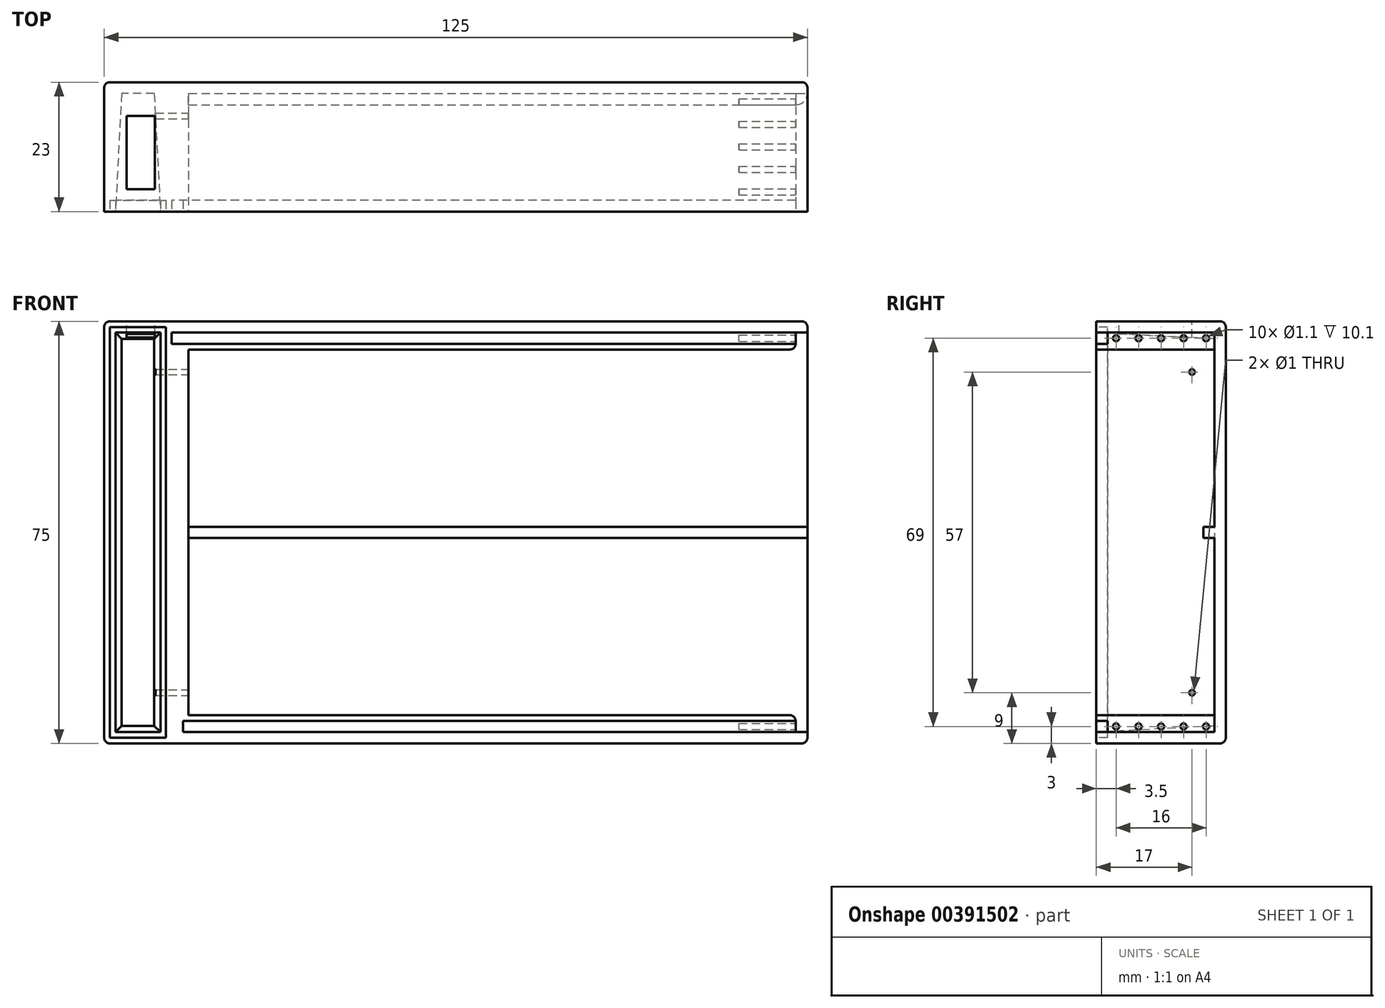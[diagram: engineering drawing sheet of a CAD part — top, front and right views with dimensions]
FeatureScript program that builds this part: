
annotation { "Feature Type Name" : "Feature", "Feature Type Description" : "" }
export const myFeature = defineFeature(function(context is Context, id is Id, definition is map)
    precondition{}
    {
        {
            var Q0;
            Q0=qCreatedBy(makeId("Front.planeOp"),FACE);
            var sketch = newSketch(context, id + "F0", { "sketchPlane" : qUnion([Q0])});
            skLineSegment(sketch, "E0.bottom", {"start": v(-62.5, 37.5) * mm, "end": v(62.5, 37.5) * mm});
            skLineSegment(sketch, "E0.top", {"start": v(-62.5, -37.5) * mm, "end": v(62.5, -37.5) * mm});
            skLineSegment(sketch, "E0.left", {"start": v(-62.5, 37.5) * mm, "end": v(-62.5, -37.5) * mm});
            skLineSegment(sketch, "E0.right", {"start": v(62.5, 37.5) * mm, "end": v(62.5, -37.5) * mm});
            skPoint(sketch, "E0.middle", {"position": v(0, 0) * mm});
            skSolve(sketch);
        }
        {
            var Q0;
            Q0 = qSketchRegion(id + "F0", true);
            extrude(context, id + "F1", {"entities" : qUnion([Q0]), "depth" : 23 * mm});
        }
        {
            var Q0;
            Q0=makeQuery(id+"F1.opExtrude","CAP_FACE",FACE,{"disambiguationData":[OSD([sQuery(id+"F0.wireOp",EDGE,"E0.bottom"),sQuery(id+"F0.wireOp",EDGE,"E0.top"),sQuery(id+"F0.wireOp",EDGE,"E0.left"),sQuery(id+"F0.wireOp",EDGE,"E0.right")])],"isStart":false});
            var sketch = newSketch(context, id + "F2", { "sketchPlane" : qUnion([Q0])});
            skLineSegment(sketch, "E1", {"start": v(-47.5, 32.5) * mm, "end": v(60.5, 32.5) * mm});
            skLineSegment(sketch, "E2", {"start": v(60.5, 32.5) * mm, "end": v(60.5, -32.5) * mm});
            skLineSegment(sketch, "E3", {"start": v(60.5, -32.5) * mm, "end": v(-47.5, -32.5) * mm});
            skLineSegment(sketch, "E4", {"start": v(-47.5, -32.5) * mm, "end": v(-47.5, 32.5) * mm});
            skSolve(sketch);
        }
        {
            var Q0;
            Q0=makeQuery(id+"F2.imprint","IMPRINT",FACE,{"disambiguationData":[TD([[makeQuery(id+"F2.imprint","IMPRINT",EDGE,{"derivedFrom":sQuery(id+"F2.wireOp",EDGE,"E1")}),-1.0]])]});
            extrude(context, id + "F3", {"entities" : qUnion([Q0]), "operationType" : NewBodyOperationType.REMOVE, "oppositeDirection" : true, "depth" : 21 * mm});
        }
        {
            var Q0;
            Q0=makeQuery(id+"F1.opExtrude","CAP_FACE",FACE,{"disambiguationData":[OSD([sQuery(id+"F0.wireOp",EDGE,"E0.bottom"),sQuery(id+"F0.wireOp",EDGE,"E0.top"),sQuery(id+"F0.wireOp",EDGE,"E0.left"),sQuery(id+"F0.wireOp",EDGE,"E0.right")])],"isStart":false});
            var sketch = newSketch(context, id + "F4", { "sketchPlane" : qUnion([Q0])});
            skLineSegment(sketch, "E5", {"start": v(-60.5, 35.5) * mm, "end": v(-52.5, 35.5) * mm});
            skLineSegment(sketch, "E6", {"start": v(-52.5, 35.5) * mm, "end": v(-52.5, -35.5) * mm});
            skLineSegment(sketch, "E7", {"start": v(-52.5, -35.5) * mm, "end": v(-60.5, -35.5) * mm});
            skLineSegment(sketch, "E8", {"start": v(-60.5, -35.5) * mm, "end": v(-60.5, 35.5) * mm});
            skSolve(sketch);
        }
        {
            var Q0;
            Q0=makeQuery(id+"F4.imprint","IMPRINT",FACE,{"disambiguationData":[TD([[makeQuery(id+"F4.imprint","IMPRINT",EDGE,{"derivedFrom":sQuery(id+"F4.wireOp",EDGE,"E5")}),-1.0]])]});
            extrude(context, id + "F5", {"entities" : qUnion([Q0]), "operationType" : NewBodyOperationType.REMOVE, "oppositeDirection" : true, "depth" : 21 * mm, "hasDraft" : true, "draftAngle" : 3 * degree, "draftPullDirection" : true});
        }
        {
            var Q0;
            Q0=makeQuery(id+"F1.opExtrude","SWEPT_FACE",FACE,{"disambiguationData":[OSD([sQuery(id+"F0.wireOp",EDGE,"E0.right")])]});
            var sketch = newSketch(context, id + "F6", { "sketchPlane" : qUnion([Q0])});
            skLineSegment(sketch, "E9", {"start": v(-23, -35.5) * mm, "end": v(-2, -35.5) * mm});
            skLineSegment(sketch, "E10", {"start": v(-2, -35.5) * mm, "end": v(-2, 35.5) * mm});
            skLineSegment(sketch, "E11", {"start": v(-2, 35.5) * mm, "end": v(-23, 35.5) * mm});
            skLineSegment(sketch, "E12", {"start": v(-23, 35.5) * mm, "end": v(-23, -35.5) * mm});
            skSolve(sketch);
        }
        {
            var Q0;
            Q0=makeQuery(id+"F6.imprint","IMPRINT",FACE,{"disambiguationData":[TD([[makeQuery(id+"F6.imprint","IMPRINT",EDGE,{"derivedFrom":sQuery(id+"F6.wireOp",EDGE,"E9")}),1.0]])]});
            extrude(context, id + "F7", {"entities" : qUnion([Q0]), "operationType" : NewBodyOperationType.REMOVE, "oppositeDirection" : true, "depth" : 2.1 * mm});
        }
        {
            var Q0;
            Q0=makeQuery(id+"F1.opExtrude","CAP_FACE",FACE,{"disambiguationData":[OSD([sQuery(id+"F0.wireOp",EDGE,"E0.bottom"),sQuery(id+"F0.wireOp",EDGE,"E0.top"),sQuery(id+"F0.wireOp",EDGE,"E0.left"),sQuery(id+"F0.wireOp",EDGE,"E0.right")])],"isStart":false});
            var sketch = newSketch(context, id + "F8", { "sketchPlane" : qUnion([Q0])});
            skLineSegment(sketch, "E13.bottom", {"start": v(60.4, 35.5) * mm, "end": v(-50.5, 35.5) * mm});
            skLineSegment(sketch, "E13.top", {"start": v(60.4, 33.5) * mm, "end": v(-50.5, 33.5) * mm});
            skLineSegment(sketch, "E13.left", {"start": v(60.4, 35.5) * mm, "end": v(60.4, 33.5) * mm});
            skLineSegment(sketch, "E13.right", {"start": v(-50.5, 35.5) * mm, "end": v(-50.5, 33.5) * mm});
            skLineSegment(sketch, "E14.bottom", {"start": v(-50.5, 33.5) * mm, "end": v(-48.5, 33.5) * mm});
            skLineSegment(sketch, "E14.top", {"start": v(-50.5, -35.5) * mm, "end": v(-48.5, -35.5) * mm});
            skLineSegment(sketch, "E14.left", {"start": v(-50.5, 33.5) * mm, "end": v(-50.5, -35.5) * mm});
            skLineSegment(sketch, "E14.right", {"start": v(-48.5, 33.5) * mm, "end": v(-48.5, -35.5) * mm});
            skLineSegment(sketch, "E15.bottom", {"start": v(60.4, -35.5) * mm, "end": v(-48.5, -35.5) * mm});
            skLineSegment(sketch, "E15.top", {"start": v(60.4, -33.5) * mm, "end": v(-48.5, -33.5) * mm});
            skLineSegment(sketch, "E15.left", {"start": v(60.4, -35.5) * mm, "end": v(60.4, -33.5) * mm});
            skLineSegment(sketch, "E15.right", {"start": v(-48.5, -35.5) * mm, "end": v(-48.5, -33.5) * mm});
            skSolve(sketch);
        }
        {
            var Q0;
            Q0=makeQuery(id+"F8.imprint","IMPRINT",FACE,{"disambiguationData":[TD([[makeQuery(id+"F8.imprint","IMPRINT",EDGE,{"derivedFrom":sQuery(id+"F8.wireOp",EDGE,"E14.bottom")}),-1.0]])]});
            var Q1;
            Q1=makeQuery(id+"F8.imprint","IMPRINT",FACE,{"disambiguationData":[TD([[makeQuery(id+"F8.imprint","IMPRINT",EDGE,{"derivedFrom":sQuery(id+"F8.wireOp",EDGE,"E13.bottom")}),1.0]])]});
            var Q2;
            Q2=makeQuery(id+"F8.imprint","IMPRINT",FACE,{"disambiguationData":[TD([[makeQuery(id+"F8.imprint","IMPRINT",EDGE,{"derivedFrom":sQuery(id+"F8.wireOp",EDGE,"E15.bottom")}),-1.0]])]});
            extrude(context, id + "F9", {"entities" : qUnion([Q0, Q1, Q2]), "operationType" : NewBodyOperationType.REMOVE, "oppositeDirection" : true, "depth" : 2 * mm});
        }
        {
            var Q0;
            Q0=makeQuery(id+"F7.boolean.opBoolean","MERGE",FACE,{"derivedFrom":[makeQuery(id+"F3.boolean.opBoolean","COPY",FACE,{"derivedFrom":makeQuery(id+"F3.opExtrude","CAP_FACE",FACE,{"disambiguationData":[OSD([sQuery(id+"F2.wireOp",EDGE,"E1"),sQuery(id+"F2.wireOp",EDGE,"E2"),sQuery(id+"F2.wireOp",EDGE,"E3"),sQuery(id+"F2.wireOp",EDGE,"E4")])],"isStart":false})}),makeQuery(id+"F7.opExtrude","SWEPT_FACE",FACE,{"disambiguationData":[OSD([sQuery(id+"F6.wireOp",EDGE,"E10")])]})]});
            var sketch = newSketch(context, id + "F10", { "sketchPlane" : qUnion([Q0])});
            skLineSegment(sketch, "E16.bottom", {"start": v(-47.5, 1) * mm, "end": v(47.5, 1) * mm});
            skLineSegment(sketch, "E16.top", {"start": v(-47.5, -1) * mm, "end": v(47.5, -1) * mm});
            skLineSegment(sketch, "E16.left", {"start": v(-47.5, 1) * mm, "end": v(-47.5, -1) * mm});
            skLineSegment(sketch, "E16.right", {"start": v(47.5, 1) * mm, "end": v(47.5, -1) * mm});
            skPoint(sketch, "E16.middle", {"position": v(0, 0) * mm});
            skLineSegment(sketch, "E17.bottom", {"start": v(47.5, 1) * mm, "end": v(62.5, 1) * mm});
            skLineSegment(sketch, "E17.top", {"start": v(47.5, -1) * mm, "end": v(62.5, -1) * mm});
            skLineSegment(sketch, "E17.right", {"start": v(62.5, 1) * mm, "end": v(62.5, -1) * mm});
            skSolve(sketch);
        }
        {
            var Q0;
            Q0 = qSketchRegion(id + "F10", true);
            var Q1;
            Q1=makeQuery(id+"F10.imprint","IMPRINT",FACE,{"disambiguationData":[TD([[makeQuery(id+"F10.imprint","IMPRINT",EDGE,{"derivedFrom":sQuery(id+"F10.wireOp",EDGE,"E16.bottom")}),-1.0]])]});
            extrude(context, id + "F11", {"entities" : qUnion([Q0, Q1]), "operationType" : NewBodyOperationType.ADD, "depth" : 2 * mm});
        }
        {
            var Q0;
            Q0=makeQuery(id+"F11.opExtrude","CAP_EDGE",EDGE,{"disambiguationData":[OSD([sQuery(id+"F10.wireOp",EDGE,"E17.right")])],"isStart":false});
            fillet(context, id + "F12", {"entities" : qUnion([Q0]), "radius" : 2 * mm, "allowEdgeOverflow" : false});
        }
        {
            var Q0;
            Q0=makeQuery(id+"F7.boolean.opBoolean","INTERSECT",EDGE,{"derivedFrom":[makeQuery(id+"F3.boolean.opBoolean","COPY",FACE,{"derivedFrom":makeQuery(id+"F3.opExtrude","SWEPT_FACE",FACE,{"disambiguationData":[OSD([sQuery(id+"F2.wireOp",EDGE,"E1")])]})}),makeQuery(id+"F7.opExtrude","CAP_FACE",FACE,{"disambiguationData":[OSD([sQuery(id+"F6.wireOp",EDGE,"E9"),sQuery(id+"F6.wireOp",EDGE,"E10"),sQuery(id+"F6.wireOp",EDGE,"E11"),sQuery(id+"F6.wireOp",EDGE,"E12")])],"isStart":false})]});
            var Q1;
            Q1=makeQuery(id+"F7.boolean.opBoolean","INTERSECT",EDGE,{"derivedFrom":[makeQuery(id+"F3.boolean.opBoolean","COPY",FACE,{"derivedFrom":makeQuery(id+"F3.opExtrude","SWEPT_FACE",FACE,{"disambiguationData":[OSD([sQuery(id+"F2.wireOp",EDGE,"E3")])]})}),makeQuery(id+"F7.opExtrude","CAP_FACE",FACE,{"disambiguationData":[OSD([sQuery(id+"F6.wireOp",EDGE,"E9"),sQuery(id+"F6.wireOp",EDGE,"E10"),sQuery(id+"F6.wireOp",EDGE,"E11"),sQuery(id+"F6.wireOp",EDGE,"E12")])],"isStart":false})]});
            fillet(context, id + "F13", {"entities" : qUnion([Q0, Q1]), "radius" : 1 * mm, "tangentPropagation" : true, "allowEdgeOverflow" : false});
        }
        {
            var Q0;
            Q0=makeQuery(id+"F1.opExtrude","SWEPT_EDGE",EDGE,{"disambiguationData":[OSD([sQuery(id+"F0.wireOp",EDGE,"E0.top"),sQuery(id+"F0.wireOp",EDGE,"E0.right")])]});
            var Q1;
            Q1=makeQuery(id+"F1.opExtrude","CAP_EDGE",EDGE,{"disambiguationData":[OSD([sQuery(id+"F0.wireOp",EDGE,"E0.right")])],"isStart":true});
            var Q2;
            Q2=makeQuery(id+"F1.opExtrude","CAP_EDGE",EDGE,{"disambiguationData":[OSD([sQuery(id+"F0.wireOp",EDGE,"E0.top")])],"isStart":true});
            var Q3;
            Q3=makeQuery(id+"F1.opExtrude","SWEPT_EDGE",EDGE,{"disambiguationData":[OSD([sQuery(id+"F0.wireOp",EDGE,"E0.bottom"),sQuery(id+"F0.wireOp",EDGE,"E0.right")])]});
            var Q4;
            Q4=makeQuery(id+"F1.opExtrude","CAP_EDGE",EDGE,{"disambiguationData":[OSD([sQuery(id+"F0.wireOp",EDGE,"E0.bottom")])],"isStart":true});
            var Q5;
            Q5=makeQuery(id+"F1.opExtrude","SWEPT_EDGE",EDGE,{"disambiguationData":[OSD([sQuery(id+"F0.wireOp",EDGE,"E0.bottom"),sQuery(id+"F0.wireOp",EDGE,"E0.left")])]});
            var Q6;
            Q6=makeQuery(id+"F1.opExtrude","CAP_EDGE",EDGE,{"disambiguationData":[OSD([sQuery(id+"F0.wireOp",EDGE,"E0.left")])],"isStart":true});
            var Q7;
            Q7=makeQuery(id+"F1.opExtrude","SWEPT_EDGE",EDGE,{"disambiguationData":[OSD([sQuery(id+"F0.wireOp",EDGE,"E0.top"),sQuery(id+"F0.wireOp",EDGE,"E0.left")])]});
            fillet(context, id + "F14", {"entities" : qUnion([Q0, Q1, Q2, Q3, Q4, Q5, Q6, Q7]), "radius" : 1 * mm, "tangentPropagation" : true, "allowEdgeOverflow" : false});
        }
        {
            var Q0;
            {var subQ0=sQuery(id+"F0.wireOp",EDGE,"E0.bottom");var subQ1=sQuery(id+"F0.wireOp",EDGE,"E0.right");var subQ2=sQuery(id+"F0.wireOp",EDGE,"E0.top");var subQ3=sQuery(id+"F0.wireOp",EDGE,"E0.left");Q0=makeQuery(id+"F9.boolean.opBoolean","SPLIT",FACE,{"disambiguationData":[TD([makeQuery(id+"F1.opExtrude","SWEPT_FACE",FACE,{"disambiguationData":[OSD([subQ0])]})])],"derivedFrom":makeQuery(id+"F1.opExtrude","CAP_FACE",FACE,{"disambiguationData":[OSD([subQ0,subQ2,subQ3,subQ1])],"isStart":false})});}
            var sketch = newSketch(context, id + "F15", { "sketchPlane" : qUnion([Q0])});
            skLineSegment(sketch, "E18.bottom", {"start": v(-60.5, 35.5) * mm, "end": v(-52.5, 35.5) * mm});
            skLineSegment(sketch, "E18.top", {"start": v(-60.5, 36.5) * mm, "end": v(-52.5, 36.5) * mm});
            skLineSegment(sketch, "E18.left", {"start": v(-60.5, 35.5) * mm, "end": v(-60.5, 36.5) * mm});
            skLineSegment(sketch, "E18.right", {"start": v(-52.5, 35.5) * mm, "end": v(-52.5, 36.5) * mm});
            skLineSegment(sketch, "E19.bottom", {"start": v(-60.5, -35.5) * mm, "end": v(-52.5, -35.5) * mm});
            skLineSegment(sketch, "E19.top", {"start": v(-60.5, -36.5) * mm, "end": v(-52.5, -36.5) * mm});
            skLineSegment(sketch, "E19.left", {"start": v(-60.5, -35.5) * mm, "end": v(-60.5, -36.5) * mm});
            skLineSegment(sketch, "E19.right", {"start": v(-52.5, -35.5) * mm, "end": v(-52.5, -36.5) * mm});
            skLineSegment(sketch, "E20.bottom", {"start": v(-60.5, -36.5) * mm, "end": v(-61.5, -36.5) * mm});
            skLineSegment(sketch, "E20.top", {"start": v(-60.5, 36.5) * mm, "end": v(-61.5, 36.5) * mm});
            skLineSegment(sketch, "E20.left", {"start": v(-60.5, -36.5) * mm, "end": v(-60.5, 36.5) * mm});
            skLineSegment(sketch, "E20.right", {"start": v(-61.5, -36.5) * mm, "end": v(-61.5, 36.5) * mm});
            skLineSegment(sketch, "E21.bottom", {"start": v(-52.5, 36.5) * mm, "end": v(-51.5, 36.5) * mm});
            skLineSegment(sketch, "E21.top", {"start": v(-52.5, -36.5) * mm, "end": v(-51.5, -36.5) * mm});
            skLineSegment(sketch, "E21.left", {"start": v(-52.5, 36.5) * mm, "end": v(-52.5, -36.5) * mm});
            skLineSegment(sketch, "E21.right", {"start": v(-51.5, 36.5) * mm, "end": v(-51.5, -36.5) * mm});
            skSolve(sketch);
        }
        {
            var Q0;
            {var subQ0=sQuery(id+"F15.wireOp",EDGE,"E18.bottom");Q0=makeQuery(id+"F15.imprint","IMPRINT",FACE,{"disambiguationData":[TD([[makeQuery(id+"F15.imprint","IMPRINT",EDGE,{"derivedFrom":subQ0}),1.0]])]});}
            var Q1;
            {var subQ3=sQuery(id+"F15.wireOp",EDGE,"E20.bottom");Q1=makeQuery(id+"F15.imprint","IMPRINT",FACE,{"disambiguationData":[TD([[makeQuery(id+"F15.imprint","IMPRINT",EDGE,{"derivedFrom":subQ3}),-1.0]])]});}
            var Q2;
            {var subQ3=sQuery(id+"F15.wireOp",EDGE,"E21.bottom");Q2=makeQuery(id+"F15.imprint","IMPRINT",FACE,{"disambiguationData":[TD([[makeQuery(id+"F15.imprint","IMPRINT",EDGE,{"derivedFrom":subQ3}),-1.0]])]});}
            var Q3;
            {var subQ0=sQuery(id+"F15.wireOp",EDGE,"E19.bottom");Q3=makeQuery(id+"F15.imprint","IMPRINT",FACE,{"disambiguationData":[TD([[makeQuery(id+"F15.imprint","IMPRINT",EDGE,{"derivedFrom":subQ0}),1.0]])]});}
            extrude(context, id + "F16", {"entities" : qUnion([Q0, Q1, Q2, Q3]), "operationType" : NewBodyOperationType.REMOVE, "oppositeDirection" : true, "depth" : 2 * mm});
        }
        {
            var Q0;
            {var subQ0=sQuery(id+"F6.wireOp",EDGE,"E9");var subQ1=sQuery(id+"F2.wireOp",EDGE,"E3");var subQ2=sQuery(id+"F6.wireOp",EDGE,"E10");Q0=makeQuery(id+"F7.boolean.opBoolean","COPY",FACE,{"disambiguationData":[TD([makeQuery(id+"F3.boolean.opBoolean","COPY",FACE,{"derivedFrom":makeQuery(id+"F3.opExtrude","SWEPT_FACE",FACE,{"disambiguationData":[OSD([subQ1])]})})])],"derivedFrom":makeQuery(id+"F7.opExtrude","CAP_FACE",FACE,{"disambiguationData":[OSD([subQ0,subQ2,sQuery(id+"F6.wireOp",EDGE,"E11"),sQuery(id+"F6.wireOp",EDGE,"E12")])],"isStart":false})});}
            var sketch = newSketch(context, id + "F17", { "sketchPlane" : qUnion([Q0])});
            skCircle(sketch, "E22", {"center": v(-19.5, -34.5) * mm, "radius": 0.55 * mm});
            skCircle(sketch, "E23", {"center": v(-15.5, -34.5) * mm, "radius": 0.55 * mm});
            skCircle(sketch, "E24", {"center": v(-11.5, -34.5) * mm, "radius": 0.55 * mm});
            skCircle(sketch, "E25", {"center": v(-3.5, -34.5) * mm, "radius": 0.55 * mm});
            skCircle(sketch, "E26", {"center": v(-7.5, -34.5) * mm, "radius": 0.55 * mm});
            skSolve(sketch);
        }
        {
            var Q0;
            Q0 = qSketchRegion(id + "F17", true);
            extrude(context, id + "F18", {"entities" : qUnion([Q0]), "operationType" : NewBodyOperationType.REMOVE, "oppositeDirection" : true, "depth" : 10.1 * mm});
        }
        {
            var Q0;
            {var subQ0=sQuery(id+"F2.wireOp",EDGE,"E1");var subQ1=sQuery(id+"F6.wireOp",EDGE,"E11");var subQ2=sQuery(id+"F6.wireOp",EDGE,"E10");Q0=makeQuery(id+"F7.boolean.opBoolean","COPY",FACE,{"disambiguationData":[TD([makeQuery(id+"F3.boolean.opBoolean","COPY",FACE,{"derivedFrom":makeQuery(id+"F3.opExtrude","SWEPT_FACE",FACE,{"disambiguationData":[OSD([subQ0])]})})])],"derivedFrom":makeQuery(id+"F7.opExtrude","CAP_FACE",FACE,{"disambiguationData":[OSD([sQuery(id+"F6.wireOp",EDGE,"E9"),subQ2,subQ1,sQuery(id+"F6.wireOp",EDGE,"E12")])],"isStart":false})});}
            var sketch = newSketch(context, id + "F19", { "sketchPlane" : qUnion([Q0])});
            skCircle(sketch, "E27", {"center": v(-19.5, 34.5) * mm, "radius": 0.55 * mm});
            skCircle(sketch, "E28", {"center": v(-15.5, 34.5) * mm, "radius": 0.55 * mm});
            skCircle(sketch, "E29", {"center": v(-11.5, 34.5) * mm, "radius": 0.55 * mm});
            skCircle(sketch, "E30", {"center": v(-7.5, 34.5) * mm, "radius": 0.55 * mm});
            skCircle(sketch, "E31", {"center": v(-3.5, 34.5) * mm, "radius": 0.55 * mm});
            skSolve(sketch);
        }
        {
            var Q0;
            Q0 = qSketchRegion(id + "F19", true);
            extrude(context, id + "F20", {"entities" : qUnion([Q0]), "operationType" : NewBodyOperationType.REMOVE, "oppositeDirection" : true, "depth" : 10.1 * mm});
        }
        {
            var Q0;
            Q0=makeQuery(id+"F3.boolean.opBoolean","COPY",FACE,{"derivedFrom":makeQuery(id+"F3.opExtrude","SWEPT_FACE",FACE,{"disambiguationData":[OSD([sQuery(id+"F2.wireOp",EDGE,"E4")])]})});
            var sketch = newSketch(context, id + "F21", { "sketchPlane" : qUnion([Q0])});
            skCircle(sketch, "E32", {"center": v(-6, -28.5) * mm, "radius": 0.5 * mm});
            skCircle(sketch, "E33", {"center": v(-6, 28.5) * mm, "radius": 0.5 * mm});
            skSolve(sketch);
        }
        {
            var Q0;
            Q0 = qSketchRegion(id + "F21", true);
            extrude(context, id + "F22", {"entities" : qUnion([Q0]), "operationType" : NewBodyOperationType.REMOVE, "oppositeDirection" : true, "depth" : 8 * mm});
        }
        {
            var Q0;
            Q0=makeQuery(id+"F1.opExtrude","SWEPT_FACE",FACE,{"disambiguationData":[OSD([sQuery(id+"F0.wireOp",EDGE,"E0.bottom")])]});
            var sketch = newSketch(context, id + "F23", { "sketchPlane" : qUnion([Q0])});
            skPoint(sketch, "E34", {"position": v(-56, -12.5) * mm});
            skLineSegment(sketch, "E35.bottom", {"start": v(-58.5, -19) * mm, "end": v(-53.5, -19) * mm});
            skLineSegment(sketch, "E35.top", {"start": v(-58.5, -6) * mm, "end": v(-53.5, -6) * mm});
            skLineSegment(sketch, "E35.left", {"start": v(-58.5, -19) * mm, "end": v(-58.5, -6) * mm});
            skLineSegment(sketch, "E35.right", {"start": v(-53.5, -19) * mm, "end": v(-53.5, -6) * mm});
            skSolve(sketch);
        }
        {
            var Q0;
            Q0 = qSketchRegion(id + "F23", true);
            extrude(context, id + "F24", {"entities" : qUnion([Q0]), "operationType" : NewBodyOperationType.REMOVE, "oppositeDirection" : true, "depth" : 3 * mm});
        }
    });
